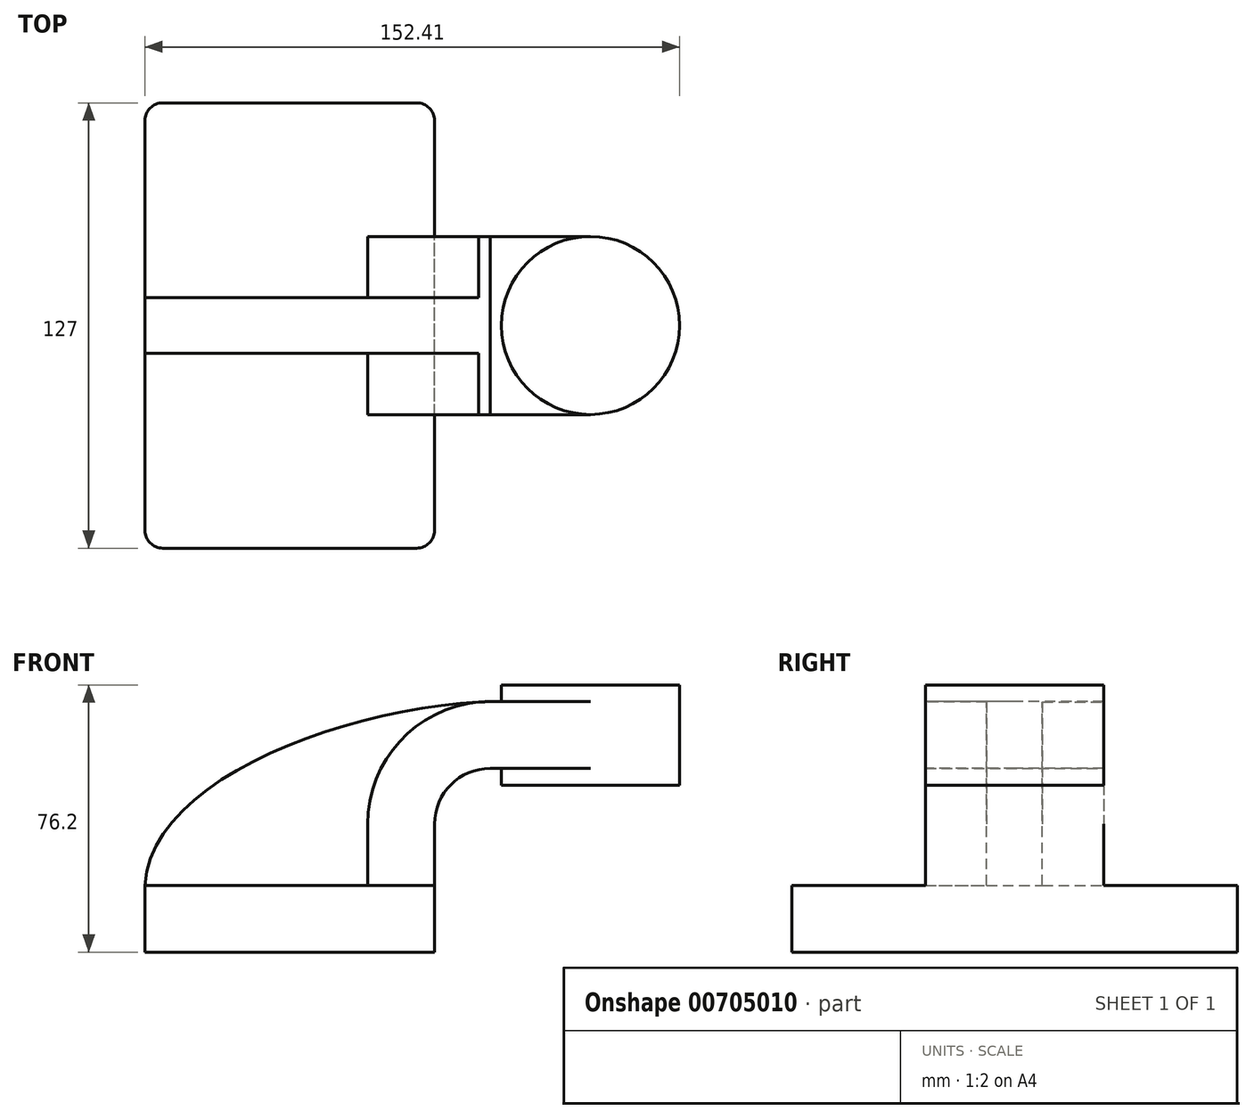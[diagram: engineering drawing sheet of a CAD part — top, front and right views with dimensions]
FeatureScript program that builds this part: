
annotation { "Feature Type Name" : "Feature", "Feature Type Description" : "" }
export const myFeature = defineFeature(function(context is Context, id is Id, definition is map)
    precondition{}
    {
        {
            var Q0;
            Q0=qCreatedBy(makeId("Front.planeOp"),FACE);
            var sketch = newSketch(context, id + "F0", { "sketchPlane" : qUnion([Q0])});
            skLineSegment(sketch, "E0.rect.bottom", {"start": v(-41.28, 9.52) * mm, "end": v(41.28, 9.52) * mm});
            skLineSegment(sketch, "E0.rect.top", {"start": v(-41.28, -9.52) * mm, "end": v(41.28, -9.52) * mm});
            skLineSegment(sketch, "E0.rect.left", {"start": v(-41.28, 9.52) * mm, "end": v(-41.28, -9.52) * mm});
            skLineSegment(sketch, "E0.rect.right", {"start": v(41.28, 9.52) * mm, "end": v(41.28, -9.52) * mm});
            skPoint(sketch, "E0.rect.middle", {"position": v(0, 0) * mm});
            skLineSegment(sketch, "E1", {"start": v(41.28, 9.52) * mm, "end": v(41.28, 27) * mm});
            skArc(sketch, "E2", {"start": v(41.28, 27) * mm, "mid": v(45.92, 38.23) * mm, "end": v(57.15, 42.88) * mm});
            skLineSegment(sketch, "E3", {"start": v(57.15, 42.88) * mm, "end": v(85.72, 42.88) * mm});
            skLineSegment(sketch, "E4.rect.bottom", {"start": v(60.32, 38.1) * mm, "end": v(111.12, 38.1) * mm});
            skLineSegment(sketch, "E4.rect.top", {"start": v(60.32, 66.68) * mm, "end": v(111.12, 66.68) * mm});
            skLineSegment(sketch, "E4.rect.left", {"start": v(60.32, 38.1) * mm, "end": v(60.32, 66.68) * mm});
            skLineSegment(sketch, "E4.rect.right", {"start": v(111.13, 38.1) * mm, "end": v(111.12, 66.68) * mm});
            skPoint(sketch, "E4.rect.middle", {"position": v(85.72, 52.39) * mm});
            skLineSegment(sketch, "E5.0", {"start": v(57.15, 61.93) * mm, "end": v(85.72, 61.93) * mm});
            skArc(sketch, "E5.1", {"start": v(22.23, 27) * mm, "mid": v(32.45, 51.7) * mm, "end": v(57.15, 61.93) * mm});
            skLineSegment(sketch, "E5.2", {"start": v(22.23, 9.52) * mm, "end": v(22.23, 27) * mm});
            skLineSegment(sketch, "E6", {"start": v(85.72, 38.1) * mm, "end": v(85.72, 66.68) * mm});
            skFitSpline(sketch, "E7", {"points": [v(-41.28, 9.53) * mm, v(57.15, 61.93) * mm], "startDerivative": vector(5.2, 92.34) * mm, "endDerivative": vector(120.92, 4.22) * mm});
            skSolve(sketch);
        }
        {
            var Q0;
            Q0=makeQuery(id+"F0.imprint","IMPRINT",FACE,{"disambiguationData":[TD([[makeQuery(id+"F0.imprint","IMPRINT",EDGE,{"derivedFrom":sQuery(id+"F0.wireOp",EDGE,"E0.rect.top")}),1.0]])]});
            extrude(context, id + "F1", {"entities" : qUnion([Q0]), "endBound" : BoundingType.SYMMETRIC, "depth" : 127 * mm});
        }
        {
            var Q0;
            {var subQ9=sQuery(id+"F0.wireOp",EDGE,"E1");Q0=makeQuery(id+"F0.imprint","IMPRINT",FACE,{"disambiguationData":[TD([[makeQuery(id+"F0.imprint","IMPRINT",EDGE,{"derivedFrom":subQ9}),1.0]])]});}
            var Q1;
            {var subQ0=sQuery(id+"F0.wireOp",EDGE,"E6");var subQ1=sQuery(id+"F0.wireOp",EDGE,"E3");var subQ2=makeQuery(id+"F0.imprint","INTERSECT",VERTEX,{"derivedFrom":[subQ1,subQ0]});Q1=makeQuery(id+"F0.imprint","IMPRINT",FACE,{"disambiguationData":[TD([[makeQuery(id+"F0.imprint","IMPRINT",EDGE,{"disambiguationData":[TD([[subQ2,1.0]])],"derivedFrom":subQ1}),1.0]])]});}
            extrude(context, id + "F2", {"entities" : qUnion([Q0, Q1]), "operationType" : NewBodyOperationType.ADD, "endBound" : BoundingType.SYMMETRIC, "depth" : 50.8 * mm});
        }
        {
            var Q0;
            {var subQ3=sQuery(id+"F0.wireOp",EDGE,"E5.2");Q0=makeQuery(id+"F0.imprint","IMPRINT",FACE,{"disambiguationData":[TD([[makeQuery(id+"F0.imprint","IMPRINT",EDGE,{"derivedFrom":subQ3}),1.0]])]});}
            extrude(context, id + "F3", {"entities" : qUnion([Q0]), "operationType" : NewBodyOperationType.ADD, "endBound" : BoundingType.SYMMETRIC, "depth" : 15.88 * mm});
        }
        {
            var Q0;
            {var subQ5=sQuery(id+"F0.wireOp",EDGE,"E4.rect.right");Q0=makeQuery(id+"F0.imprint","IMPRINT",FACE,{"disambiguationData":[TD([[makeQuery(id+"F0.imprint","IMPRINT",EDGE,{"derivedFrom":subQ5}),1.0]])]});}
            var Q1;
            Q1=sQuery(id+"F0.wireOp",EDGE,"E6");
            revolve(context, id + "F4", {"operationType" : NewBodyOperationType.ADD, "entities" : qUnion([Q0]), "axis" : qUnion([Q1]), "revolveType" : RevolveType.FULL});
        }
        {
            var Q0;
            Q0=makeQuery(id+"F1.opExtrude","CAP_EDGE",EDGE,{"disambiguationData":[OSD([sQuery(id+"F0.wireOp",EDGE,"E0.rect.right")])],"isStart":false});
            var Q1;
            Q1=makeQuery(id+"F1.opExtrude","CAP_EDGE",EDGE,{"disambiguationData":[OSD([sQuery(id+"F0.wireOp",EDGE,"E0.rect.left")])],"isStart":false});
            var Q2;
            Q2=makeQuery(id+"F1.opExtrude","CAP_EDGE",EDGE,{"disambiguationData":[OSD([sQuery(id+"F0.wireOp",EDGE,"E0.rect.right")])],"isStart":true});
            var Q3;
            Q3=makeQuery(id+"F1.opExtrude","CAP_EDGE",EDGE,{"disambiguationData":[OSD([sQuery(id+"F0.wireOp",EDGE,"E0.rect.left")])],"isStart":true});
            fillet(context, id + "F5", {"entities" : qUnion([Q0, Q1, Q2, Q3]), "radius" : 5.08 * mm, "tangentPropagation" : true, "allowEdgeOverflow" : false});
        }
        {
            var Q0;
            Q0=makeQuery(id+"F1.opExtrude","SWEPT_BODY",BODY,{"disambiguationData":[OSD([sQuery(id+"F0.wireOp",EDGE,"E0.rect.bottom"),sQuery(id+"F0.wireOp",EDGE,"E0.rect.top"),sQuery(id+"F0.wireOp",EDGE,"E0.rect.left"),sQuery(id+"F0.wireOp",EDGE,"E0.rect.right")])]});
            transform(context, id + "F6", {"entities" : qUnion([Q0]), "transformType" : TransformType.TRANSLATION_3D, "dx" : -91.44 * mm, "dy" : 91.44 * mm, "dz" : 58.67 * mm, "makeCopy" : false});
        }
    });
